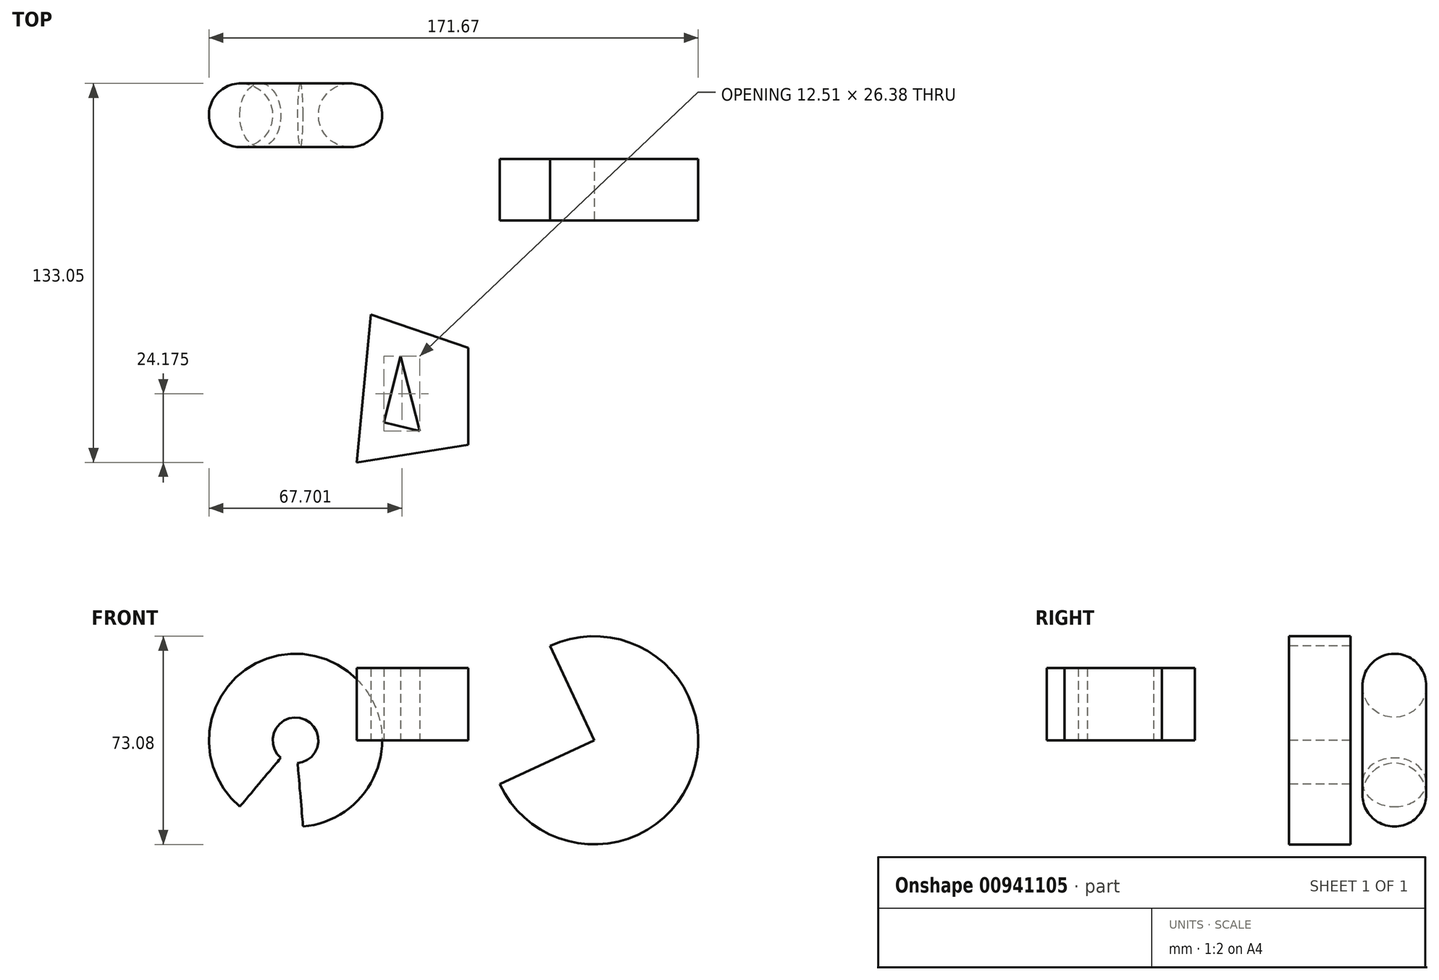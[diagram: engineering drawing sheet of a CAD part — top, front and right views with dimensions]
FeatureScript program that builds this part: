
annotation { "Feature Type Name" : "Feature", "Feature Type Description" : "" }
export const myFeature = defineFeature(function(context is Context, id is Id, definition is map)
    precondition{}
    {
        {
            var Q0;
            Q0=qCreatedBy(makeId("Top.planeOp"),FACE);
            var sketch = newSketch(context, id + "F0", { "sketchPlane" : qUnion([Q0])});
            skCircle(sketch, "E0", {"center": v(-62.28, 52.52) * mm, "radius": 11.18 * mm});
            skLineSegment(sketch, "E1.bottom", {"start": v(23.25, 37.16) * mm, "end": v(59.79, 37.16) * mm});
            skLineSegment(sketch, "E1.top", {"start": v(23.25, 15.57) * mm, "end": v(59.79, 15.57) * mm});
            skLineSegment(sketch, "E1.left", {"start": v(23.25, 37.16) * mm, "end": v(23.25, 15.57) * mm});
            skLineSegment(sketch, "E1.right", {"start": v(59.79, 37.16) * mm, "end": v(59.79, 15.57) * mm});
            skLineSegment(sketch, "E2", {"start": v(-55, -17.45) * mm, "end": v(-20.95, -29.08) * mm});
            skLineSegment(sketch, "E3", {"start": v(-20.95, -29.08) * mm, "end": v(-20.95, -63.13) * mm});
            skLineSegment(sketch, "E4", {"start": v(-20.95, -63.13) * mm, "end": v(-59.98, -69.35) * mm});
            skLineSegment(sketch, "E5", {"start": v(-59.98, -69.35) * mm, "end": v(-55, -17.45) * mm});
            skLineSegment(sketch, "E6", {"start": v(-44.62, -31.99) * mm, "end": v(-50.43, -55.24) * mm});
            skLineSegment(sketch, "E7", {"start": v(-50.43, -55.24) * mm, "end": v(-37.93, -58.36) * mm});
            skLineSegment(sketch, "E8", {"start": v(-37.93, -58.36) * mm, "end": v(-44.62, -31.99) * mm});
            skLineSegment(sketch, "E9", {"start": v(-81.5, 60.81) * mm, "end": v(-81.5, 30.26) * mm, "construction": true});
            skSolve(sketch);
        }
        {
            var Q0;
            Q0=makeQuery(id+"F0.imprint","IMPRINT",FACE,{"disambiguationData":[TD([[makeQuery(id+"F0.imprint","IMPRINT",EDGE,{"derivedFrom":sQuery(id+"F0.wireOp",EDGE,"E0")}),1.0]])]});
            var Q1;
            Q1=sQuery(id+"F0.wireOp",EDGE,"E9");
            revolve(context, id + "F1", {"surfaceOperationType" : NewSurfaceOperationType.NEW, "entities" : qUnion([Q0]), "axis" : qUnion([Q1]), "revolveType" : RevolveType.TWO_DIRECTIONS, "angle" : 230 * degree, "angleBack" : 275 * degree});
        }
        {
            var Q0;
            Q0=makeQuery(id+"F0.imprint","IMPRINT",FACE,{"disambiguationData":[TD([[makeQuery(id+"F0.imprint","IMPRINT",EDGE,{"derivedFrom":sQuery(id+"F0.wireOp",EDGE,"E2")}),-1.0]])]});
            extrude(context, id + "F2", {"entities" : qUnion([Q0]), "depth" : 25.4 * mm, "offsetDistance" : 25.4 * mm});
        }
        {
            var Q0;
            Q0=makeQuery(id+"F0.imprint","IMPRINT",FACE,{"disambiguationData":[TD([[makeQuery(id+"F0.imprint","IMPRINT",EDGE,{"derivedFrom":sQuery(id+"F0.wireOp",EDGE,"E1.bottom")}),-1.0]])]});
            var Q1;
            Q1=sQuery(id+"F0.wireOp",EDGE,"E1.left");
            revolve(context, id + "F3", {"surfaceOperationType" : NewSurfaceOperationType.NEW, "entities" : qUnion([Q0]), "axis" : qUnion([Q1]), "revolveType" : RevolveType.TWO_DIRECTIONS, "angle" : 115 * degree, "angleBack" : 205 * degree});
        }
    });
